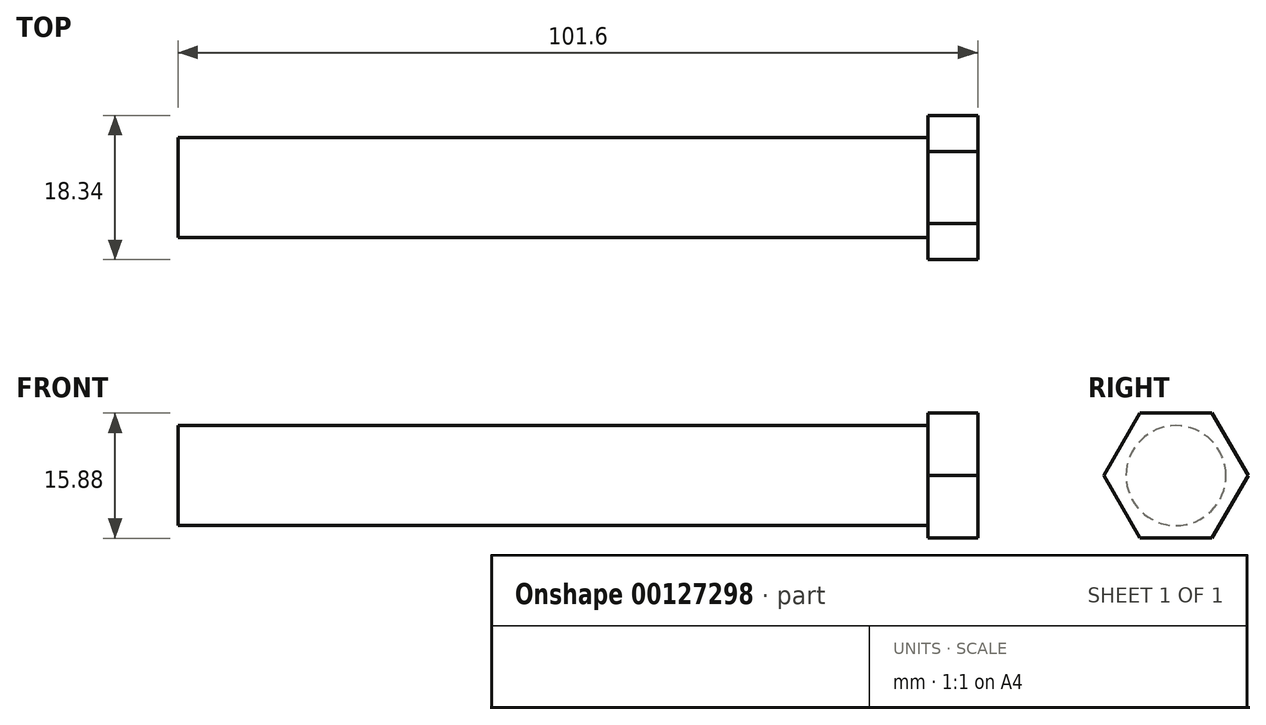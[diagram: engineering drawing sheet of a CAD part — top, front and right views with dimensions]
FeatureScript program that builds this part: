
annotation { "Feature Type Name" : "Feature", "Feature Type Description" : "" }
export const myFeature = defineFeature(function(context is Context, id is Id, definition is map)
    precondition{}
    {
        {
            var Q0;
            Q0=qCreatedBy(makeId("Right.planeOp"),FACE);
            var sketch = newSketch(context, id + "F0", { "sketchPlane" : qUnion([Q0])});
            skCircle(sketch, "E0", {"center": v(0, 0) * mm, "radius": 6.35 * mm});
            skSolve(sketch);
        }
        {
            var Q0;
            Q0 = qSketchRegion(id + "F0", true);
            extrude(context, id + "F1", {"entities" : qUnion([Q0]), "depth" : 95.25 * mm});
        }
        {
            var Q0;
            Q0=makeQuery(id+"F1.opExtrude","CAP_FACE",FACE,{"disambiguationData":[OSD([sQuery(id+"F0.wireOp",EDGE,"E0")])],"isStart":false});
            var sketch = newSketch(context, id + "F2", { "sketchPlane" : qUnion([Q0])});
            skLineSegment(sketch, "E1", {"start": v(-4.58, 7.94) * mm, "end": v(4.58, 7.94) * mm});
            skLineSegment(sketch, "E2.1.0", {"start": v(-9.17, 0) * mm, "end": v(-4.58, 7.94) * mm});
            skLineSegment(sketch, "E2.2.0", {"start": v(-4.58, -7.94) * mm, "end": v(-9.17, 0) * mm});
            skLineSegment(sketch, "E2.3.0", {"start": v(4.58, -7.94) * mm, "end": v(-4.58, -7.94) * mm});
            skLineSegment(sketch, "E2.4.0", {"start": v(9.17, 0) * mm, "end": v(4.58, -7.94) * mm});
            skLineSegment(sketch, "E2.5.0", {"start": v(4.58, 7.94) * mm, "end": v(9.17, 0) * mm});
            skPoint(sketch, "E2.center", {"position": v(0, 0) * mm});
            skPoint(sketch, "E3.orphan", {"position": v(-6.35, 7.94) * mm});
            skPoint(sketch, "E4.orphan", {"position": v(-3.7, 9.47) * mm});
            skPoint(sketch, "E5.orphan", {"position": v(3.7, 9.47) * mm});
            skPoint(sketch, "E6.orphan", {"position": v(6.35, 7.94) * mm});
            skPoint(sketch, "E7.orphan", {"position": v(10.05, 1.53) * mm});
            skPoint(sketch, "E8.orphan", {"position": v(10.05, -1.53) * mm});
            skPoint(sketch, "E9.orphan", {"position": v(3.7, -9.47) * mm});
            skPoint(sketch, "E10.orphan", {"position": v(6.35, -7.94) * mm});
            skPoint(sketch, "E11.orphan", {"position": v(-3.7, -9.47) * mm});
            skPoint(sketch, "E12.orphan", {"position": v(-6.35, -7.94) * mm});
            skPoint(sketch, "E13.orphan", {"position": v(-10.05, -1.53) * mm});
            skPoint(sketch, "E14.orphan", {"position": v(-10.05, 1.53) * mm});
            skSolve(sketch);
        }
        {
            var Q0;
            Q0 = qSketchRegion(id + "F2", true);
            extrude(context, id + "F3", {"entities" : qUnion([Q0]), "operationType" : NewBodyOperationType.ADD, "depth" : 6.35 * mm});
        }
    });
